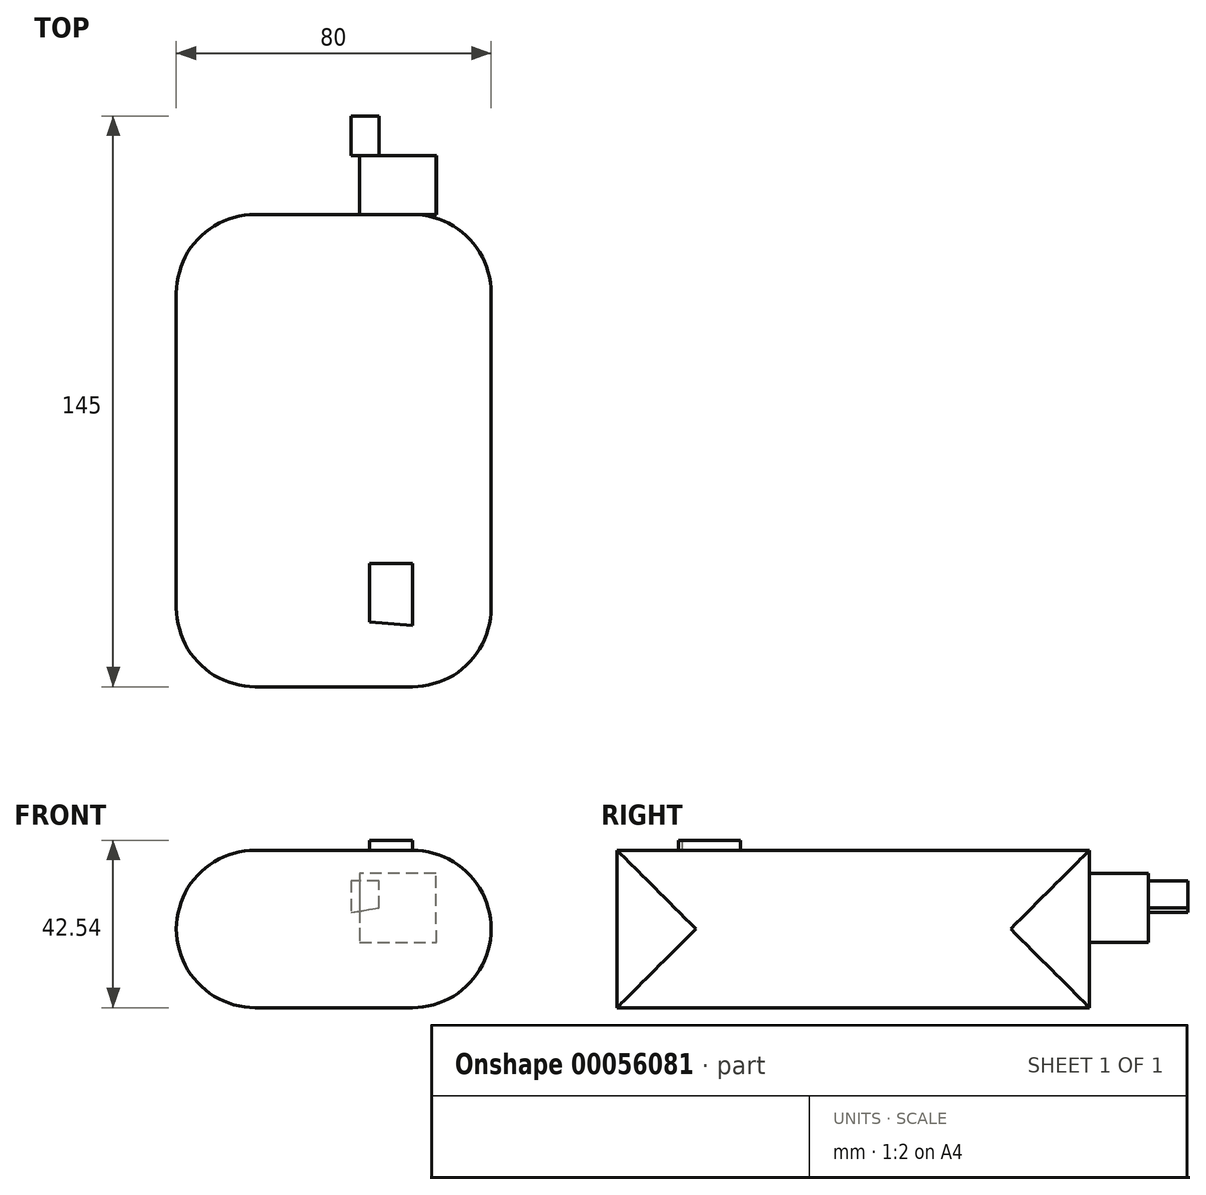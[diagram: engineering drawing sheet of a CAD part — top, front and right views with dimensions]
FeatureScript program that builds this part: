
annotation { "Feature Type Name" : "Feature", "Feature Type Description" : "" }
export const myFeature = defineFeature(function(context is Context, id is Id, definition is map)
    precondition{}
    {
        {
            var Q0;
            Q0=qCreatedBy(makeId("Top.planeOp"),FACE);
            var sketch = newSketch(context, id + "F0", { "sketchPlane" : qUnion([Q0])});
            skLineSegment(sketch, "E0", {"start": v(-128.82, 0.07) * mm, "end": v(-128.82, -119.93) * mm});
            skLineSegment(sketch, "E1", {"start": v(-128.82, -119.93) * mm, "end": v(-48.82, -119.93) * mm});
            skLineSegment(sketch, "E2", {"start": v(-48.82, -119.93) * mm, "end": v(-48.82, 0.07) * mm});
            skLineSegment(sketch, "E3", {"start": v(-48.82, 0.07) * mm, "end": v(-128.82, 0.07) * mm});
            skSolve(sketch);
        }
        {
            var Q0;
            Q0=qSketchRegion(id+"F0",true);
            extrude(context, id + "F1", {"entities" : qUnion([Q0]), "depth" : 40 * mm});
        }
        {
            var Q0;
            Q0=makeQuery(id+"F1.opExtrude","SWEPT_FACE",FACE,{"disambiguationData":[OSD([sQuery(id+"F0.wireOp",EDGE,"E2")])]});
            var Q1;
            Q1=makeQuery(id+"F1.opExtrude","SWEPT_FACE",FACE,{"disambiguationData":[OSD([sQuery(id+"F0.wireOp",EDGE,"E0")])]});
            fillet(context, id + "F2", {"entities" : qUnion([Q0, Q1]), "radius" : 20 * mm, "tangentPropagation" : true, "allowEdgeOverflow" : false});
        }
        {
            var Q0;
            Q0=makeQuery(id+"F1.opExtrude","CAP_FACE",FACE,{"disambiguationData":[OSD([sQuery(id+"F0.wireOp",EDGE,"E0"),sQuery(id+"F0.wireOp",EDGE,"E1"),sQuery(id+"F0.wireOp",EDGE,"E2"),sQuery(id+"F0.wireOp",EDGE,"E3")])],"isStart":false});
            var sketch = newSketch(context, id + "F3", { "sketchPlane" : qUnion([Q0])});
            skLineSegment(sketch, "E4", {"start": v(-68.82, -104.34) * mm, "end": v(-68.82, -88.63) * mm});
            skLineSegment(sketch, "E5", {"start": v(-68.82, -88.63) * mm, "end": v(-79.76, -88.63) * mm});
            skLineSegment(sketch, "E6", {"start": v(-79.76, -88.63) * mm, "end": v(-79.76, -103.52) * mm});
            skLineSegment(sketch, "E7", {"start": v(-79.76, -103.52) * mm, "end": v(-68.82, -104.34) * mm});
            skSolve(sketch);
        }
        {
            var Q0;
            Q0=makeQuery(id+"F3.imprint","IMPRINT",FACE,{"disambiguationData":[TD([[makeQuery(id+"F3.imprint","IMPRINT",EDGE,{"derivedFrom":sQuery(id+"F3.wireOp",EDGE,"E4")}),1.0]])]});
            extrude(context, id + "F4", {"entities" : qUnion([Q0]), "operationType" : NewBodyOperationType.ADD, "depth" : 2.54 * mm});
        }
        {
            var Q0;
            Q0=makeQuery(id+"F1.opExtrude","SWEPT_FACE",FACE,{"disambiguationData":[OSD([sQuery(id+"F0.wireOp",EDGE,"E3")])]});
            var sketch = newSketch(context, id + "F5", { "sketchPlane" : qUnion([Q0])});
            skLineSegment(sketch, "E8", {"start": v(62.86, 34.12) * mm, "end": v(82.26, 34.12) * mm});
            skLineSegment(sketch, "E9", {"start": v(82.26, 34.12) * mm, "end": v(82.26, 16.64) * mm});
            skLineSegment(sketch, "E10", {"start": v(82.26, 16.64) * mm, "end": v(62.74, 16.64) * mm});
            skLineSegment(sketch, "E11", {"start": v(62.74, 16.64) * mm, "end": v(62.86, 34.12) * mm});
            skSolve(sketch);
        }
        {
            var Q0;
            Q0=qSketchRegion(id+"F5",true);
            extrude(context, id + "F6", {"entities" : qUnion([Q0]), "depth" : 15 * mm});
        }
        {
            var Q0;
            Q0=makeQuery(id+"F6.opExtrude","CAP_FACE",FACE,{"disambiguationData":[OSD([sQuery(id+"F5.wireOp",EDGE,"E8"),sQuery(id+"F5.wireOp",EDGE,"E9"),sQuery(id+"F5.wireOp",EDGE,"E10"),sQuery(id+"F5.wireOp",EDGE,"E11")])],"isStart":false});
            var sketch = newSketch(context, id + "F7", { "sketchPlane" : qUnion([Q0])});
            skLineSegment(sketch, "E12", {"start": v(77.32, 25.38) * mm, "end": v(77.32, 32.25) * mm});
            skPoint(sketch, "E12.startSnap0", {"position": v(62.8, 25.38) * mm});
            skLineSegment(sketch, "E13", {"start": v(77.32, 32.25) * mm, "end": v(84.36, 32.25) * mm});
            skLineSegment(sketch, "E14", {"start": v(84.36, 32.25) * mm, "end": v(84.36, 24.15) * mm});
            skLineSegment(sketch, "E15", {"start": v(84.36, 24.15) * mm, "end": v(77.32, 25.38) * mm});
            skSolve(sketch);
        }
        {
            var Q0;
            Q0=qSketchRegion(id+"F7",true);
            extrude(context, id + "F8", {"entities" : qUnion([Q0]), "operationType" : NewBodyOperationType.ADD, "depth" : 10 * mm});
        }
    });
